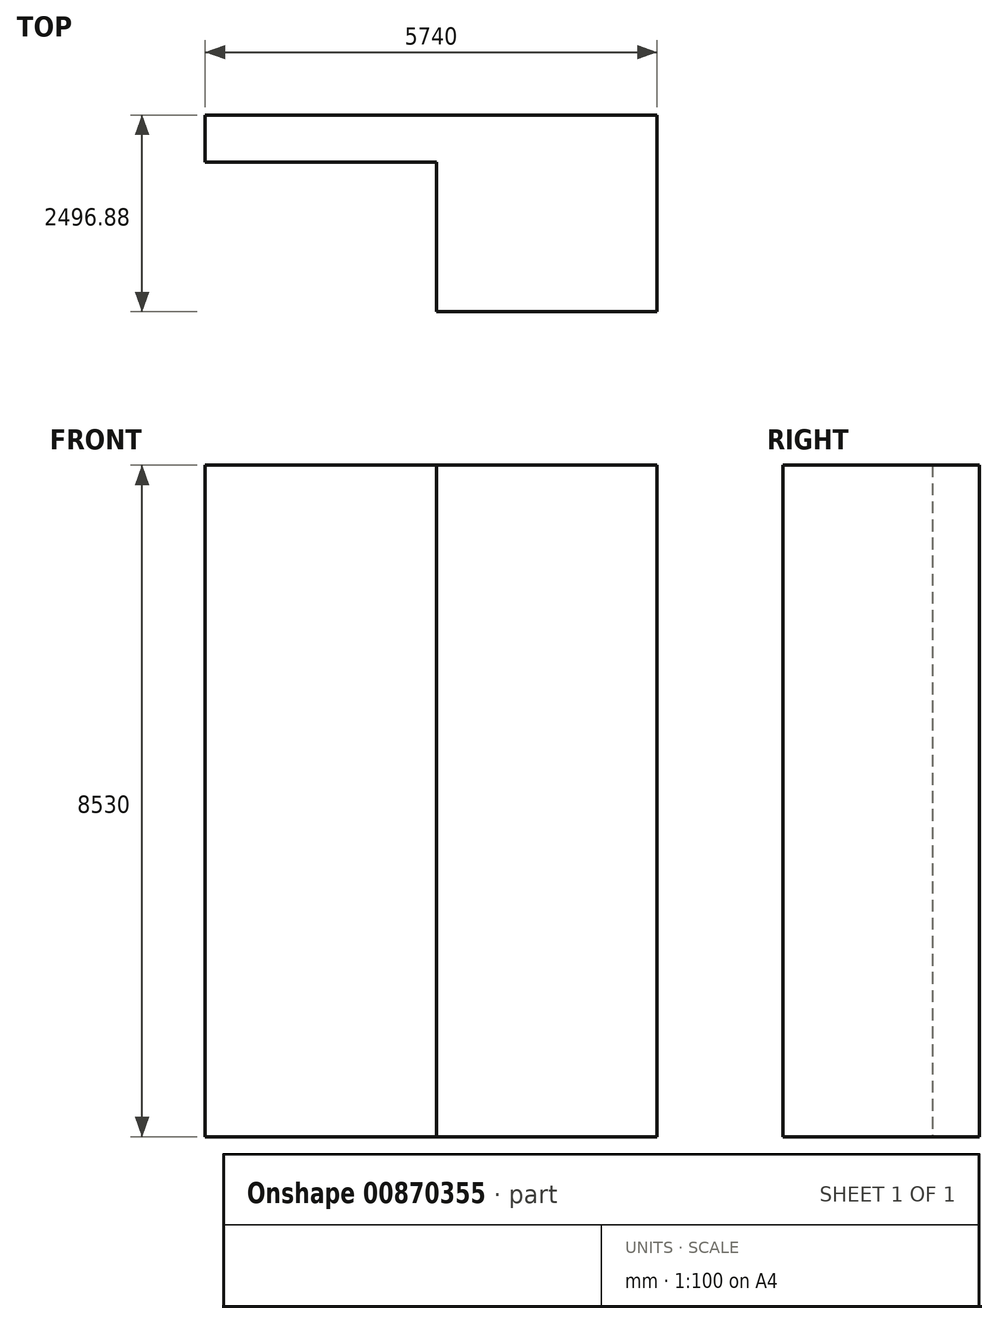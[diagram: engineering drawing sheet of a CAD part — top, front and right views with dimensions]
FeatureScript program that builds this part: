
annotation { "Feature Type Name" : "Feature", "Feature Type Description" : "" }
export const myFeature = defineFeature(function(context is Context, id is Id, definition is map)
    precondition{}
    {
        {
            var Q0;
            Q0=qCreatedBy(makeId("Top.planeOp"),FACE);
            var sketch = newSketch(context, id + "F0", { "sketchPlane" : qUnion([Q0])});
            skLineSegment(sketch, "E0", {"start": v(-2832.87, 772.16) * mm, "end": v(107.13, 772.16) * mm});
            skLineSegment(sketch, "E1", {"start": v(107.13, 772.16) * mm, "end": v(107.13, -1127.84) * mm});
            skLineSegment(sketch, "E2", {"start": v(107.13, -1127.84) * mm, "end": v(2907.13, -1127.84) * mm});
            skLineSegment(sketch, "E3", {"start": v(-2832.87, 772.16) * mm, "end": v(-2832.87, 1369.04) * mm});
            skLineSegment(sketch, "E4", {"start": v(-2832.87, 1369.04) * mm, "end": v(2907.13, 1369.04) * mm});
            skLineSegment(sketch, "E5", {"start": v(2907.13, 1369.04) * mm, "end": v(2907.13, -1127.84) * mm});
            skSolve(sketch);
        }
        {
            var Q0;
            Q0=makeQuery(id+"F0.imprint","IMPRINT",FACE,{"disambiguationData":[TD([[makeQuery(id+"F0.imprint","IMPRINT",EDGE,{"derivedFrom":sQuery(id+"F0.wireOp",EDGE,"E0")}),1.0]])]});
            extrude(context, id + "F1", {"entities" : qUnion([Q0]), "depth" : 8530 * mm, "offsetDistance" : 25 * mm});
        }
    });
